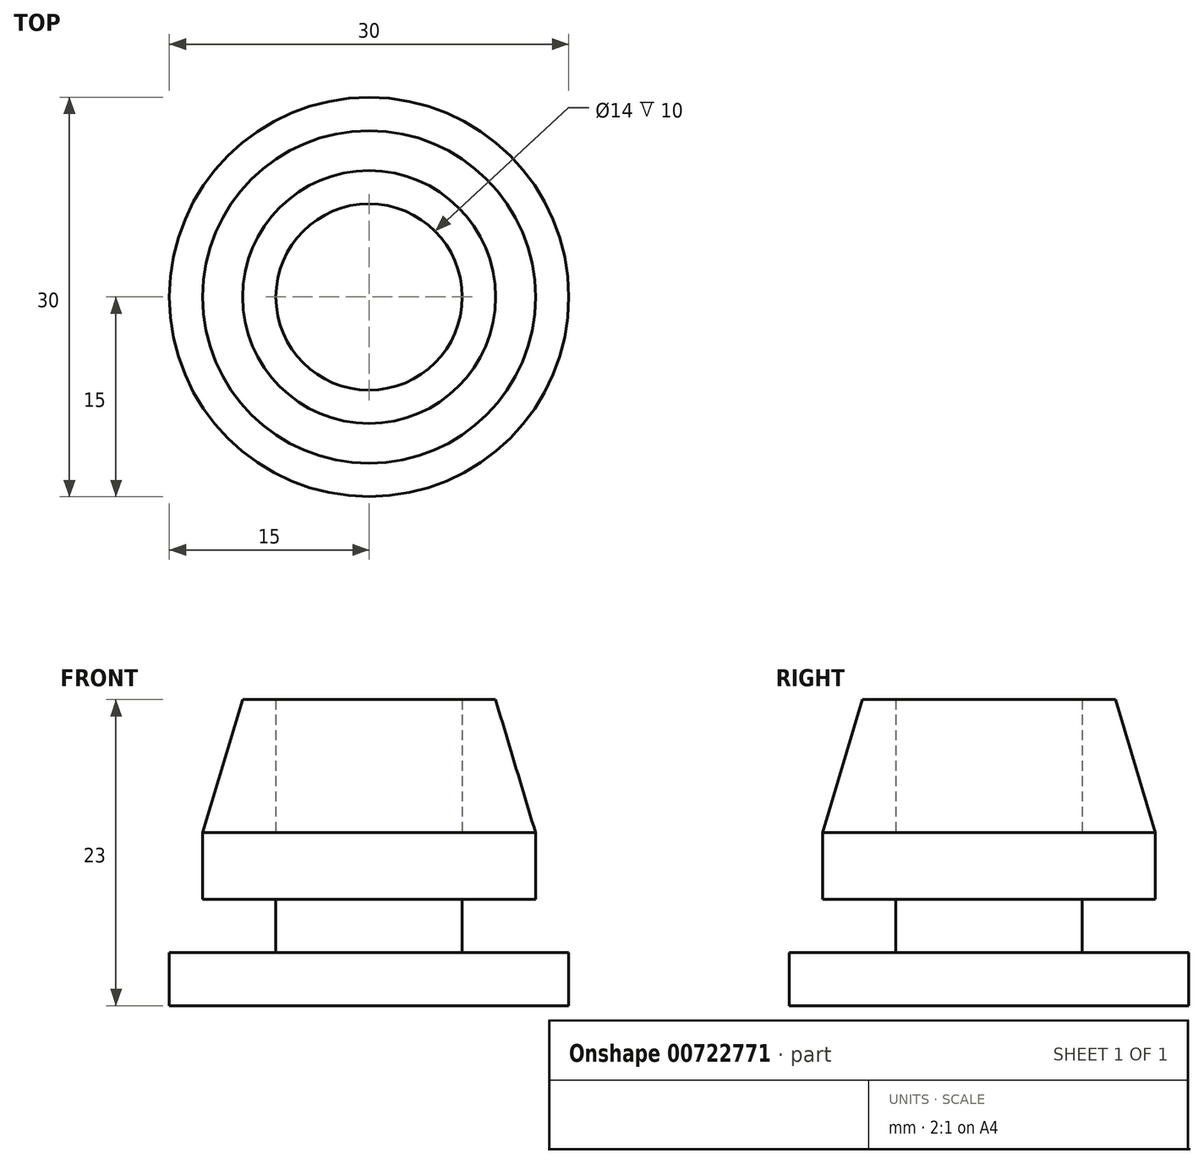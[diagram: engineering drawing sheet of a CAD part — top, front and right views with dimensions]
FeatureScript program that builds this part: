
annotation { "Feature Type Name" : "Feature", "Feature Type Description" : "" }
export const myFeature = defineFeature(function(context is Context, id is Id, definition is map)
    precondition{}
    {
        {
            var Q0;
            Q0=qCreatedBy(makeId("Top.planeOp"),FACE);
            var sketch = newSketch(context, id + "F0", { "sketchPlane" : qUnion([Q0])});
            skCircle(sketch, "E0", {"center": v(0, 0) * mm, "radius": 15 * mm});
            skSolve(sketch);
        }
        {
            var Q0;
            Q0=makeQuery(id+"F0.imprint","IMPRINT",FACE,{"disambiguationData":[TD([[makeQuery(id+"F0.imprint","IMPRINT",EDGE,{"derivedFrom":sQuery(id+"F0.wireOp",EDGE,"E0")}),1.0]])]});
            extrude(context, id + "F1", {"entities" : qUnion([Q0]), "depth" : 4 * mm, "offsetDistance" : 25 * mm});
        }
        {
            var Q0;
            Q0=makeQuery(id+"F1.opExtrude","CAP_FACE",FACE,{"disambiguationData":[OSD([sQuery(id+"F0.wireOp",EDGE,"E0")])],"isStart":false});
            var sketch = newSketch(context, id + "F2", { "sketchPlane" : qUnion([Q0])});
            skCircle(sketch, "E1", {"center": v(0, 0) * mm, "radius": 7 * mm});
            skSolve(sketch);
        }
        {
            var Q0;
            Q0=makeQuery(id+"F2.imprint","IMPRINT",FACE,{"disambiguationData":[TD([[makeQuery(id+"F2.imprint","IMPRINT",EDGE,{"derivedFrom":sQuery(id+"F2.wireOp",EDGE,"E1")}),1.0]])]});
            extrude(context, id + "F3", {"entities" : qUnion([Q0]), "operationType" : NewBodyOperationType.ADD, "depth" : 4 * mm, "offsetDistance" : 25 * mm});
        }
        {
            var Q0;
            Q0=makeQuery(id+"F3.opExtrude","CAP_FACE",FACE,{"disambiguationData":[OSD([sQuery(id+"F2.wireOp",EDGE,"E1")])],"isStart":false});
            var sketch = newSketch(context, id + "F4", { "sketchPlane" : qUnion([Q0])});
            skCircle(sketch, "E2", {"center": v(0, 0) * mm, "radius": 12.5 * mm});
            skSolve(sketch);
        }
        {
            var Q0;
            Q0=makeQuery(id+"F4.imprint","IMPRINT",FACE,{"disambiguationData":[TD([[makeQuery(id+"F4.imprint","IMPRINT",EDGE,{"derivedFrom":sQuery(id+"F4.wireOp",EDGE,"E2")}),1.0]])]});
            extrude(context, id + "F5", {"entities" : qUnion([Q0]), "operationType" : NewBodyOperationType.ADD, "depth" : 15 * mm, "offsetDistance" : 25 * mm});
        }
        {
            var Q0;
            Q0=makeQuery(id+"F5.opExtrude","CAP_EDGE",EDGE,{"disambiguationData":[OSD([sQuery(id+"F4.wireOp",EDGE,"E2")])],"isStart":false});
            chamfer(context, id + "F6", {"entities" : qUnion([Q0]), "chamferType" : ChamferType.TWO_OFFSETS, "width1" : 3 * mm, "oppositeDirection" : false, "width2" : 10 * mm, "tangentPropagation" : true});
        }
        {
            var Q0;
            Q0=makeQuery(id+"F3.opExtrude","CAP_FACE",FACE,{"disambiguationData":[OSD([sQuery(id+"F2.wireOp",EDGE,"E1")])],"isStart":false});
            extrude(context, id + "F7", {"entities" : qUnion([Q0]), "operationType" : NewBodyOperationType.ADD, "depth" : 5 * mm, "offsetDistance" : 25 * mm});
        }
    });
